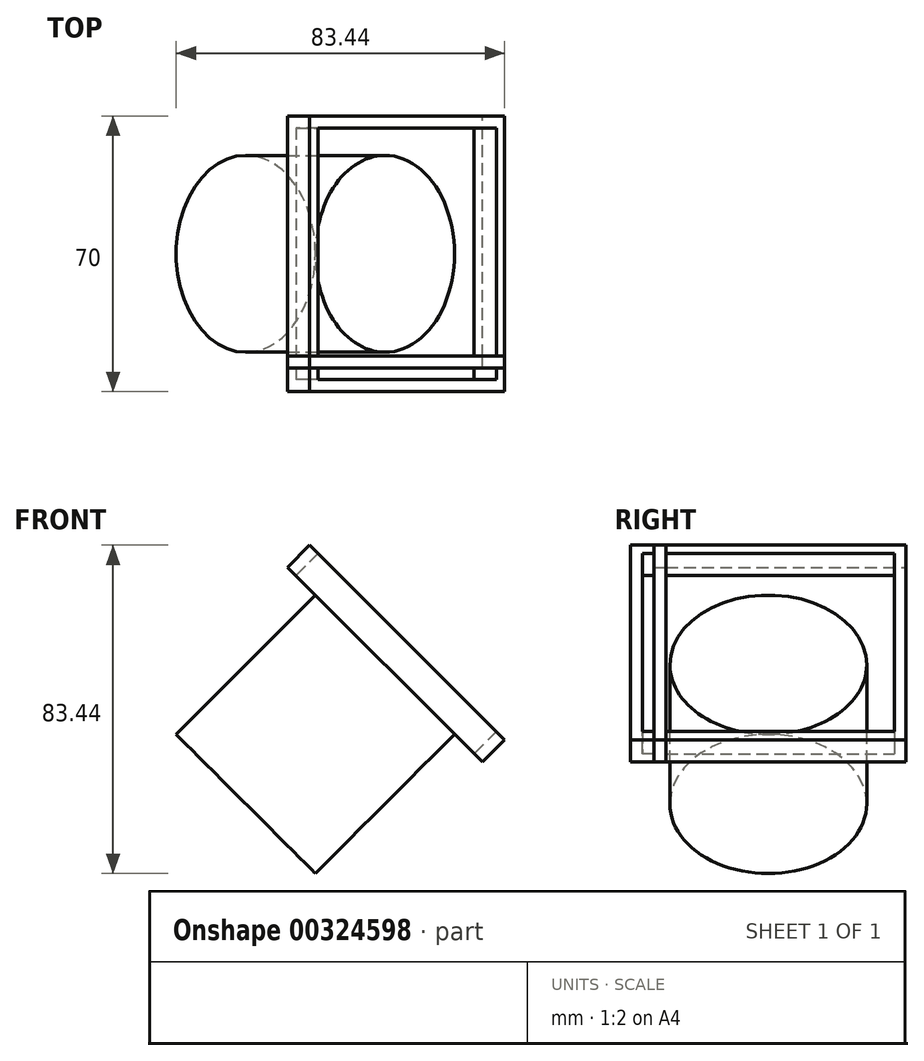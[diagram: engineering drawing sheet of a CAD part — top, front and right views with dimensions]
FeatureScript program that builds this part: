
annotation { "Feature Type Name" : "Feature", "Feature Type Description" : "" }
export const myFeature = defineFeature(function(context is Context, id is Id, definition is map)
    precondition{}
    {
        {
            assignVariable(context, id + "F0", {"name" : "PT", "anyValue" : 70});
        }
        {
            assignVariable(context, id + "F1", {"name" : "PL", "anyValue" : 150});
        }
        {
            assignVariable(context, id + "F2", {"name" : "WT", "anyValue" : 3});
        }
        {
            var Q0;
            Q0=qCreatedBy(makeId("Front.planeOp"),FACE);
            var sketch = newSketch(context, id + "F3", { "sketchPlane" : qUnion([Q0])});
            skLineSegment(sketch, "E0", {"start": v(0, 0) * mm, "end": v(81.32, 81.32) * mm, "construction": true});
            skLineSegment(sketch, "E1", {"start": v(0, 0) * mm, "end": v(-24.75, 24.75) * mm});
            skLineSegment(sketch, "E2", {"start": v(-24.75, 24.75) * mm, "end": v(81.32, 130.81) * mm});
            skLineSegment(sketch, "E3.MirrorCS", {"start": v(24.75, -24.75) * mm, "end": v(130.81, 81.32) * mm});
            skLineSegment(sketch, "E4.MirrorCS", {"start": v(0, 0) * mm, "end": v(24.75, -24.75) * mm});
            skLineSegment(sketch, "E5", {"start": v(81.32, 130.81) * mm, "end": v(130.81, 81.32) * mm});
            skLineSegment(sketch, "E6", {"start": v(81.32, 130.81) * mm, "end": v(-24.75, 236.88) * mm});
            skLineSegment(sketch, "E7", {"start": v(-24.75, 236.88) * mm, "end": v(-74.25, 187.38) * mm});
            skLineSegment(sketch, "E8", {"start": v(-74.25, 187.38) * mm, "end": v(31.82, 81.32) * mm});
            skLineSegment(sketch, "E9", {"start": v(81.32, 81.32) * mm, "end": v(-24.75, 187.38) * mm, "construction": true});
            skLineSegment(sketch, "E10", {"start": v(-24.75, 187.38) * mm, "end": v(81.32, 293.45) * mm, "construction": true});
            skLineSegment(sketch, "E11", {"start": v(-24.75, 236.88) * mm, "end": v(81.32, 342.95) * mm});
            skLineSegment(sketch, "E12", {"start": v(81.32, 342.95) * mm, "end": v(130.81, 293.45) * mm});
            skLineSegment(sketch, "E13", {"start": v(130.81, 293.45) * mm, "end": v(24.75, 187.38) * mm});
            skLineSegment(sketch, "E14.0", {"start": v(81.32, 126.57) * mm, "end": v(126.57, 81.32) * mm});
            skLineSegment(sketch, "E14.1", {"start": v(-20.5, 24.75) * mm, "end": v(81.32, 126.57) * mm});
            skLineSegment(sketch, "E14.2", {"start": v(24.75, -20.5) * mm, "end": v(126.57, 81.32) * mm});
            skLineSegment(sketch, "E14.3", {"start": v(2.12, 2.12) * mm, "end": v(24.75, -20.5) * mm});
            skLineSegment(sketch, "E14.4", {"start": v(2.12, 2.12) * mm, "end": v(-20.5, 24.75) * mm});
            skLineSegment(sketch, "E15", {"start": v(75.66, 125.16) * mm, "end": v(-12.02, 125.16) * mm});
            skLineSegment(sketch, "E16", {"start": v(75.66, 125.16) * mm, "end": v(75.66, 30.4) * mm, "construction": true});
            skSolve(sketch);
        }
        {
            var Q0;
            Q0=sQuery(id+"F3.wireOp",EDGE,"E5");
            cPlane(context, id + "F4", {"entities" : qUnion([Q0]), "cplaneType" : CPlaneType.LINE_ANGLE, "offset" : 25 * mm, "angle" : 90 * degree, "width" : 150 * mm, "height" : 150 * mm});
        }
        {
            var Q0;
            Q0=qCreatedBy(id+"F4.planeOp",FACE);
            var sketch = newSketch(context, id + "F5", { "sketchPlane" : qUnion([Q0])});
            skLineSegment(sketch, "E17.0", {"start": v(-35, 0) * mm, "end": v(35, 0) * mm});
            skSolve(sketch);
        }
        {
            var Q0;
            Q0=qCreatedBy(makeId("Front.planeOp"),FACE);
            cPlane(context, id + "F6", {"entities" : qUnion([Q0]), "cplaneType" : CPlaneType.OFFSET, "offset" : (getVariable(context, 'PT')) * mm, "width" : 150 * mm, "height" : 150 * mm});
        }
        {
            var Q0;
            Q0=qCreatedBy(id+"F6.planeOp",FACE);
            var sketch = newSketch(context, id + "F7", { "sketchPlane" : qUnion([Q0])});
            skLineSegment(sketch, "E18.0", {"start": v(-24.75, 24.75) * mm, "end": v(81.32, 130.81) * mm});
            skLineSegment(sketch, "E19.0", {"start": v(24.75, -24.75) * mm, "end": v(130.81, 81.32) * mm});
            skLineSegment(sketch, "E20.0", {"start": v(0, 0) * mm, "end": v(24.75, -24.75) * mm});
            skLineSegment(sketch, "E20.1", {"start": v(0, 0) * mm, "end": v(-24.75, 24.75) * mm});
            skLineSegment(sketch, "E21.0", {"start": v(81.32, 130.81) * mm, "end": v(130.81, 81.32) * mm});
            skLineSegment(sketch, "E22.0", {"start": v(-20.5, 24.75) * mm, "end": v(81.32, 126.57) * mm});
            skLineSegment(sketch, "E22.1", {"start": v(2.12, 2.12) * mm, "end": v(-20.5, 24.75) * mm});
            skLineSegment(sketch, "E22.2", {"start": v(2.12, 2.12) * mm, "end": v(24.75, -20.5) * mm});
            skLineSegment(sketch, "E22.3", {"start": v(24.75, -20.5) * mm, "end": v(126.57, 81.32) * mm});
            skLineSegment(sketch, "E22.4", {"start": v(81.32, 126.57) * mm, "end": v(126.57, 81.32) * mm});
            skSolve(sketch);
        }
        {
            var Q0;
            Q0=qCreatedBy(id+"F4.planeOp",FACE);
            cPlane(context, id + "F8", {"entities" : qUnion([Q0]), "cplaneType" : CPlaneType.OFFSET, "offset" : (getVariable(context, 'PL')) * mm, "oppositeDirection" : true, "width" : 150 * mm, "height" : 150 * mm});
        }
        {
            var Q0;
            Q0=qCreatedBy(id+"F8.planeOp",FACE);
            var sketch = newSketch(context, id + "F9", { "sketchPlane" : qUnion([Q0])});
            skLineSegment(sketch, "E23.0", {"start": v(0, 0) * mm, "end": v(35, 0) * mm});
            skLineSegment(sketch, "E23.1", {"start": v(0, 0) * mm, "end": v(-35, 0) * mm});
            skLineSegment(sketch, "E23.2", {"start": v(0, -70) * mm, "end": v(-35, -70) * mm});
            skLineSegment(sketch, "E23.3", {"start": v(0, -70) * mm, "end": v(35, -70) * mm});
            skLineSegment(sketch, "E24", {"start": v(-35, -70) * mm, "end": v(-35, 0) * mm});
            skLineSegment(sketch, "E25", {"start": v(35, 0) * mm, "end": v(35, -70) * mm});
            skLineSegment(sketch, "E26.0", {"start": v(0, -67) * mm, "end": v(-32, -67) * mm});
            skLineSegment(sketch, "E26.1", {"start": v(0, -3) * mm, "end": v(-32, -3) * mm});
            skLineSegment(sketch, "E26.2", {"start": v(0, -3) * mm, "end": v(32, -3) * mm});
            skLineSegment(sketch, "E26.3", {"start": v(-32, -67) * mm, "end": v(-32, -3) * mm});
            skLineSegment(sketch, "E26.4", {"start": v(32, -3) * mm, "end": v(32, -67) * mm});
            skLineSegment(sketch, "E26.5", {"start": v(0, -67) * mm, "end": v(32, -67) * mm});
            skLineSegment(sketch, "E27", {"start": v(-35, 0) * mm, "end": v(35, -70) * mm, "construction": true});
            skCircle(sketch, "E28", {"center": v(0, -35) * mm, "radius": 25 * mm});
            skSolve(sketch);
        }
        {
            var Q0;
            Q0=qCreatedBy(id+"F4.planeOp",FACE);
            var sketch = newSketch(context, id + "F10", { "sketchPlane" : qUnion([Q0])});
            skLineSegment(sketch, "E29.0", {"start": v(-35, -70) * mm, "end": v(35, -70) * mm});
            skLineSegment(sketch, "E29.1", {"start": v(-35, 0) * mm, "end": v(35, 0) * mm});
            skLineSegment(sketch, "E30.0", {"start": v(-35, -70) * mm, "end": v(-35, 0) * mm});
            skLineSegment(sketch, "E31.0", {"start": v(-32, -67) * mm, "end": v(-32, -3) * mm});
            skLineSegment(sketch, "E31.1", {"start": v(0, -67) * mm, "end": v(-32, -67) * mm});
            skLineSegment(sketch, "E31.2", {"start": v(0, -67) * mm, "end": v(32, -67) * mm});
            skLineSegment(sketch, "E31.3", {"start": v(32, -3) * mm, "end": v(32, -67) * mm});
            skLineSegment(sketch, "E31.4", {"start": v(0, -3) * mm, "end": v(32, -3) * mm});
            skLineSegment(sketch, "E31.5", {"start": v(0, -3) * mm, "end": v(-32, -3) * mm});
            skLineSegment(sketch, "E32.0", {"start": v(35, 0) * mm, "end": v(35, -70) * mm});
            skLineSegment(sketch, "E33", {"start": v(32, -67) * mm, "end": v(-32, -3) * mm, "construction": true});
            skCircle(sketch, "E34", {"center": v(0, -35) * mm, "radius": 25 * mm});
            skSolve(sketch);
        }
        {
            var Q0;
            Q0=sQuery(id+"F7.wireOp",EDGE,"E18.0");
            cPlane(context, id + "F11", {"entities" : qUnion([Q0]), "cplaneType" : CPlaneType.LINE_ANGLE, "offset" : 25 * mm, "angle" : 90 * degree, "width" : 150 * mm, "height" : 150 * mm});
        }
        {
            var Q0;
            Q0=qCreatedBy(id+"F11.planeOp",FACE);
            var sketch = newSketch(context, id + "F12", { "sketchPlane" : qUnion([Q0])});
            skLineSegment(sketch, "E35.0", {"start": v(70, 0) * mm, "end": v(70, 150) * mm});
            skLineSegment(sketch, "E35.1", {"start": v(70, 0) * mm, "end": v(0, 0) * mm});
            skLineSegment(sketch, "E35.2", {"start": v(0, 0) * mm, "end": v(0, 150) * mm});
            skLineSegment(sketch, "E35.3", {"start": v(70, 150) * mm, "end": v(0, 150) * mm});
            skLineSegment(sketch, "E36.0", {"start": v(67, 3) * mm, "end": v(67, 147) * mm});
            skLineSegment(sketch, "E36.1", {"start": v(67, 3) * mm, "end": v(3, 3) * mm});
            skLineSegment(sketch, "E36.2", {"start": v(3, 3) * mm, "end": v(3, 147) * mm});
            skLineSegment(sketch, "E36.3", {"start": v(67, 147) * mm, "end": v(3, 147) * mm});
            skLineSegment(sketch, "E37", {"start": v(67, 142) * mm, "end": v(3, 142) * mm});
            skSolve(sketch);
        }
        {
            var Q0;
            Q0=sQuery(id+"F7.wireOp",EDGE,"E19.0");
            cPlane(context, id + "F13", {"entities" : qUnion([Q0]), "cplaneType" : CPlaneType.LINE_ANGLE, "offset" : 25 * mm, "angle" : 90 * degree, "width" : 150 * mm, "height" : 150 * mm});
        }
        {
            var Q0;
            Q0=qCreatedBy(id+"F4.planeOp",FACE);
            cPlane(context, id + "F14", {"entities" : qUnion([Q0]), "cplaneType" : CPlaneType.OFFSET, "offset" : (getVariable(context, 'WT') + 5) * mm, "oppositeDirection" : true, "width" : 150 * mm, "height" : 150 * mm});
        }
        {
            var Q0;
            Q0=qCreatedBy(id+"F14.planeOp",FACE);
            var sketch = newSketch(context, id + "F15", { "sketchPlane" : qUnion([Q0])});
            skLineSegment(sketch, "E38.0", {"start": v(-35, -70) * mm, "end": v(35, -70) * mm});
            skLineSegment(sketch, "E38.1", {"start": v(-35, -70) * mm, "end": v(-35, 0) * mm});
            skLineSegment(sketch, "E38.2", {"start": v(-35, 0) * mm, "end": v(35, 0) * mm});
            skLineSegment(sketch, "E38.3", {"start": v(0, -3) * mm, "end": v(-32, -3) * mm});
            skLineSegment(sketch, "E38.4", {"start": v(0, -3) * mm, "end": v(32, -3) * mm});
            skLineSegment(sketch, "E38.5", {"start": v(-32, -67) * mm, "end": v(-32, -3) * mm});
            skLineSegment(sketch, "E38.6", {"start": v(0, -67) * mm, "end": v(-32, -67) * mm});
            skCircle(sketch, "E38.7", {"center": v(0, -35) * mm, "radius": 25 * mm});
            skLineSegment(sketch, "E38.8", {"start": v(0, -67) * mm, "end": v(32, -67) * mm});
            skLineSegment(sketch, "E38.9", {"start": v(32, -3) * mm, "end": v(32, -67) * mm});
            skLineSegment(sketch, "E38.10", {"start": v(35, 0) * mm, "end": v(35, -70) * mm});
            skLineSegment(sketch, "E39", {"start": v(-29, 0) * mm, "end": v(-29, -70) * mm});
            skLineSegment(sketch, "E40", {"start": v(-26, -70) * mm, "end": v(-26, 0) * mm});
            skSolve(sketch);
        }
        {
            var Q0;
            Q0=makeQuery(id+"F15.imprint","IMPRINT",FACE,{"disambiguationData":[TD([[makeQuery(id+"F15.imprint","IMPRINT",EDGE,{"derivedFrom":sQuery(id+"F15.wireOp",EDGE,"E38.7")}),1.0]])]});
            extrude(context, id + "F16", {"entities" : qUnion([Q0]), "oppositeDirection" : true, "depth" : 50 * mm});
        }
        {
            var Q0;
            {var subQ0=sQuery(id+"F15.wireOp",EDGE,"E40");var subQ1=sQuery(id+"F15.wireOp",EDGE,"E38.3");var subQ2=makeQuery(id+"F15.imprint","INTERSECT",VERTEX,{"derivedFrom":[subQ1,subQ0]});Q0=makeQuery(id+"F15.imprint","IMPRINT",FACE,{"disambiguationData":[TD([[makeQuery(id+"F15.imprint","IMPRINT",EDGE,{"disambiguationData":[TD([[subQ2,-1.0]])],"derivedFrom":subQ1}),1.0]])]});}
            var Q1;
            {var subQ0=sQuery(id+"F15.wireOp",EDGE,"E39");var subQ1=sQuery(id+"F15.wireOp",EDGE,"E38.0");var subQ2=makeQuery(id+"F15.imprint","INTERSECT",VERTEX,{"derivedFrom":[subQ1,subQ0]});Q1=makeQuery(id+"F15.imprint","IMPRINT",FACE,{"disambiguationData":[TD([[makeQuery(id+"F15.imprint","IMPRINT",EDGE,{"disambiguationData":[TD([[subQ2,-1.0]])],"derivedFrom":subQ1}),1.0]])]});}
            var Q2;
            {var subQ0=sQuery(id+"F15.wireOp",EDGE,"E39");var subQ1=sQuery(id+"F15.wireOp",EDGE,"E38.2");var subQ2=makeQuery(id+"F15.imprint","INTERSECT",VERTEX,{"derivedFrom":[subQ1,subQ0]});Q2=makeQuery(id+"F15.imprint","IMPRINT",FACE,{"disambiguationData":[TD([[makeQuery(id+"F15.imprint","IMPRINT",EDGE,{"disambiguationData":[TD([[subQ2,-1.0]])],"derivedFrom":subQ1}),-1.0]])]});}
            extrude(context, id + "F17", {"entities" : qUnion([Q0, Q1, Q2]), "depth" : 8 * mm});
        }
        {
            var Q0;
            {var subQ5=sQuery(id+"F15.wireOp",EDGE,"E38.1");Q0=makeQuery(id+"F15.imprint","IMPRINT",FACE,{"disambiguationData":[TD([[makeQuery(id+"F15.imprint","IMPRINT",EDGE,{"derivedFrom":subQ5}),-1.0]])]});}
            var Q1;
            {var subQ0=sQuery(id+"F15.wireOp",EDGE,"E38.4");Q1=makeQuery(id+"F15.imprint","IMPRINT",FACE,{"disambiguationData":[TD([[makeQuery(id+"F15.imprint","IMPRINT",EDGE,{"derivedFrom":subQ0}),1.0]])]});}
            extrude(context, id + "F18", {"entities" : qUnion([Q0, Q1]), "depth" : 8 * mm});
        }
    });
